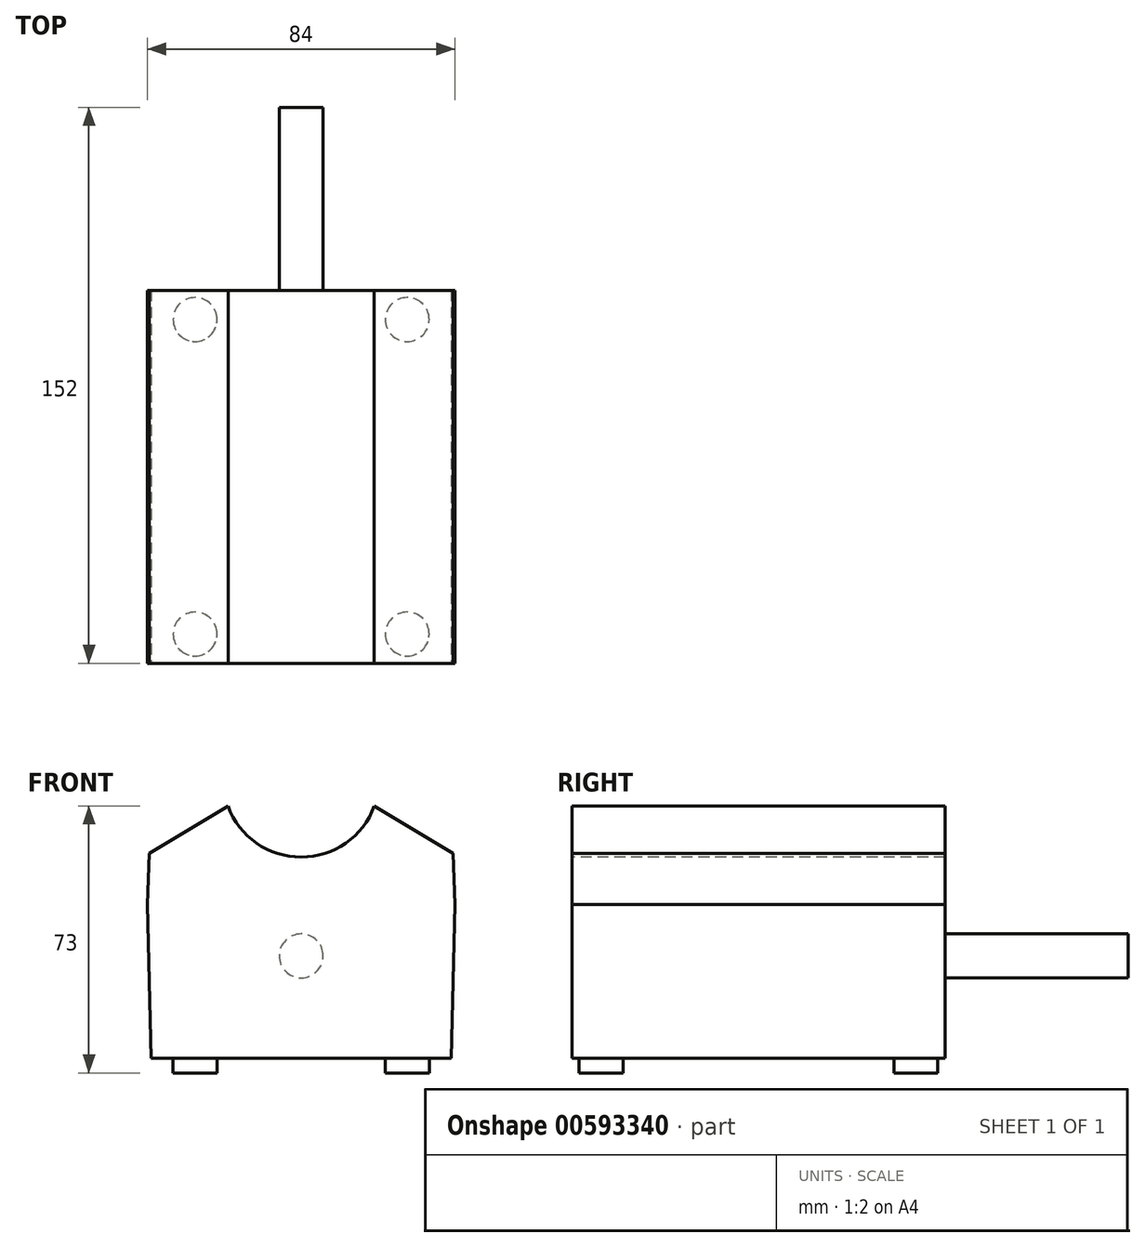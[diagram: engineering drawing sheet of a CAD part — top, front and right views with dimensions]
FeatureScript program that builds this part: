
annotation { "Feature Type Name" : "Feature", "Feature Type Description" : "" }
export const myFeature = defineFeature(function(context is Context, id is Id, definition is map)
    precondition{}
    {
        {
            var Q0;
            Q0=qCreatedBy(makeId("Front.planeOp"),FACE);
            var sketch = newSketch(context, id + "F0", { "sketchPlane" : qUnion([Q0])});
            skLineSegment(sketch, "E0", {"start": v(0, 4) * mm, "end": v(-41, 4) * mm});
            skLineSegment(sketch, "E1", {"start": v(-42, 46) * mm, "end": v(-41, 4) * mm});
            skLineSegment(sketch, "E2", {"start": v(-42, 46) * mm, "end": v(-41.5, 60) * mm});
            skLineSegment(sketch, "E3", {"start": v(-41.5, 60) * mm, "end": v(-20, 73) * mm});
            skLineSegment(sketch, "E4.MirrorCS", {"start": v(41.5, 60) * mm, "end": v(20, 73) * mm});
            skLineSegment(sketch, "E5.MirrorCS", {"start": v(42, 46) * mm, "end": v(41.5, 60) * mm});
            skLineSegment(sketch, "E6.MirrorCS", {"start": v(42, 46) * mm, "end": v(41, 4) * mm});
            skLineSegment(sketch, "E7.MirrorCS", {"start": v(0, 4) * mm, "end": v(41, 4) * mm});
            skArc(sketch, "E8", {"start": v(-20, 73) * mm, "mid": v(0, 59) * mm, "end": v(20, 73) * mm});
            skSolve(sketch);
        }
        {
            var Q0;
            Q0 = qSketchRegion(id + "F0", true);
            extrude(context, id + "F1", {"entities" : qUnion([Q0]), "oppositeDirection" : true, "depth" : 102 * mm, "offsetDistance" : 25 * mm});
        }
        {
            var Q0;
            Q0=makeQuery(id+"F1.opExtrude","CAP_FACE",FACE,{"disambiguationData":[OSD([sQuery(id+"F0.wireOp",EDGE,"E0"),sQuery(id+"F0.wireOp",EDGE,"E1"),sQuery(id+"F0.wireOp",EDGE,"E2"),sQuery(id+"F0.wireOp",EDGE,"E3"),sQuery(id+"F0.wireOp",EDGE,"E4.MirrorCS"),sQuery(id+"F0.wireOp",EDGE,"E5.MirrorCS"),sQuery(id+"F0.wireOp",EDGE,"E6.MirrorCS"),sQuery(id+"F0.wireOp",EDGE,"E7.MirrorCS"),sQuery(id+"F0.wireOp",EDGE,"E8")])],"isStart":false});
            var sketch = newSketch(context, id + "F2", { "sketchPlane" : qUnion([Q0])});
            skCircle(sketch, "E9", {"center": v(0, 32) * mm, "radius": 6 * mm});
            skSolve(sketch);
        }
        {
            var Q0;
            Q0 = qSketchRegion(id + "F2", true);
            extrude(context, id + "F3", {"entities" : qUnion([Q0]), "operationType" : NewBodyOperationType.ADD, "depth" : 50 * mm, "offsetDistance" : 25 * mm});
        }
        {
            var Q0;
            Q0=makeQuery(id+"F1.opExtrude","SWEPT_FACE",FACE,{"disambiguationData":[OSD([sQuery(id+"F0.wireOp",EDGE,"E0"),sQuery(id+"F0.wireOp",EDGE,"E7.MirrorCS")])]});
            var sketch = newSketch(context, id + "F4", { "sketchPlane" : qUnion([Q0])});
            skLineSegment(sketch, "E10.bottom", {"start": v(29, -94) * mm, "end": v(-29, -94) * mm, "construction": true});
            skLineSegment(sketch, "E10.top", {"start": v(29, -8) * mm, "end": v(-29, -8) * mm, "construction": true});
            skLineSegment(sketch, "E10.left", {"start": v(29, -94) * mm, "end": v(29, -8) * mm, "construction": true});
            skLineSegment(sketch, "E10.right", {"start": v(-29, -94) * mm, "end": v(-29, -8) * mm, "construction": true});
            skCircle(sketch, "E11", {"center": v(29, -94) * mm, "radius": 6 * mm});
            skCircle(sketch, "E12", {"center": v(-29, -94) * mm, "radius": 6 * mm});
            skCircle(sketch, "E13", {"center": v(-29, -8) * mm, "radius": 6 * mm});
            skCircle(sketch, "E14", {"center": v(29, -8) * mm, "radius": 6 * mm});
            skLineSegment(sketch, "E15", {"start": v(0, -94) * mm, "end": v(0, -102) * mm, "construction": true});
            skLineSegment(sketch, "E16", {"start": v(0, -8) * mm, "end": v(0, 0) * mm, "construction": true});
            skSolve(sketch);
        }
        {
            var Q0;
            Q0 = qSketchRegion(id + "F4", true);
            extrude(context, id + "F5", {"entities" : qUnion([Q0]), "operationType" : NewBodyOperationType.ADD, "depth" : 4 * mm, "offsetDistance" : 25 * mm});
        }
    });
